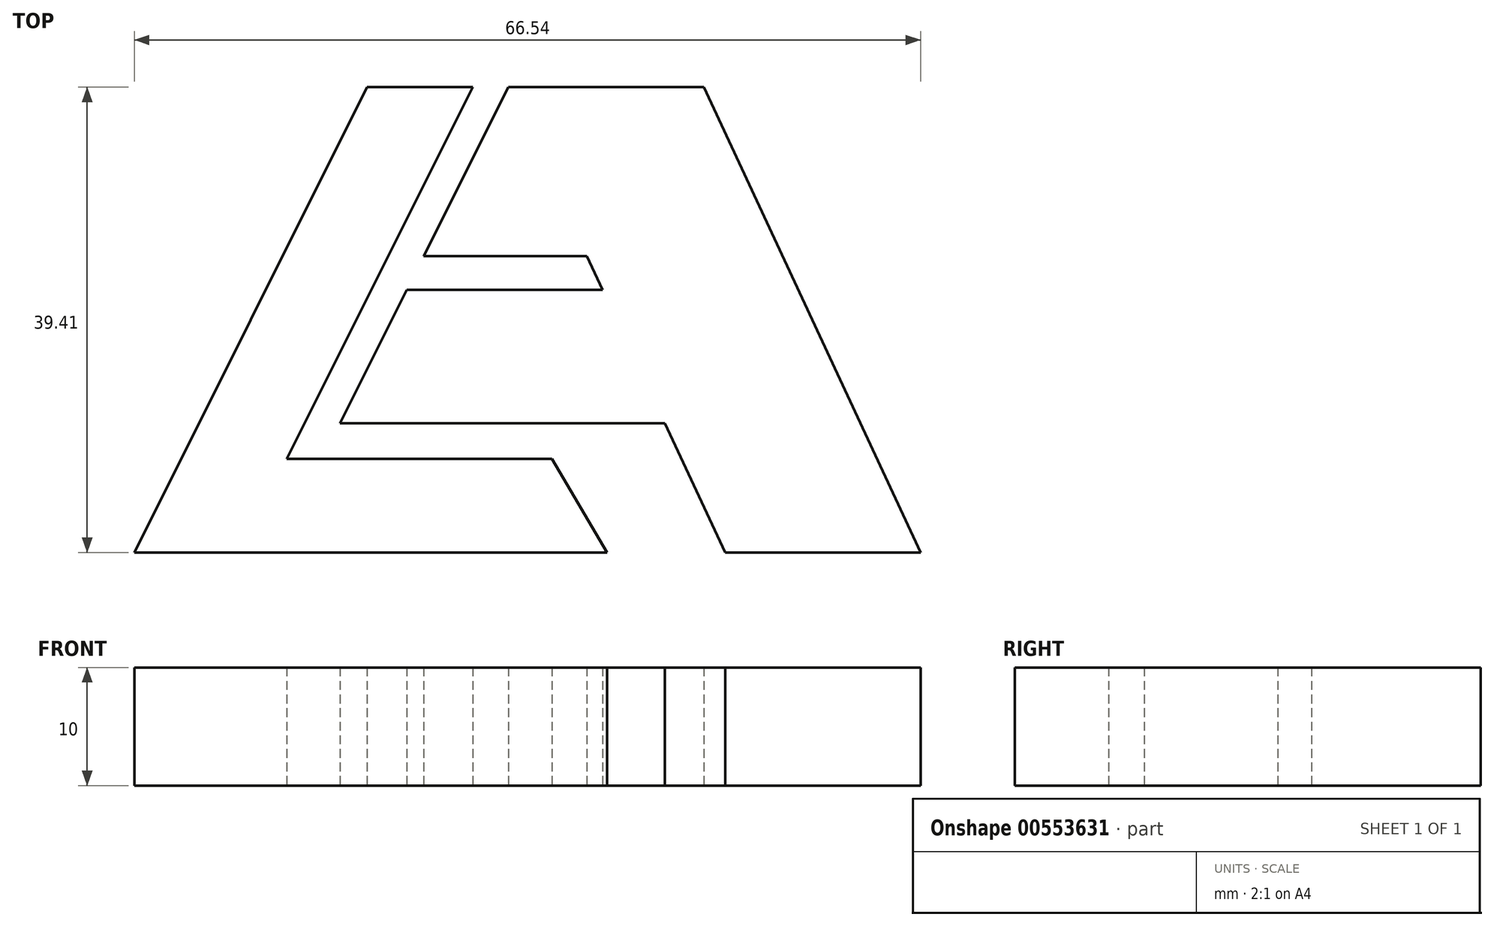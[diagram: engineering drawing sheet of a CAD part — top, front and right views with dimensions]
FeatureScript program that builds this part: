
annotation { "Feature Type Name" : "Feature", "Feature Type Description" : "" }
export const myFeature = defineFeature(function(context is Context, id is Id, definition is map)
    precondition{}
    {
        {
            var Q0;
            Q0=qCreatedBy(makeId("Top.planeOp"),FACE);
            var sketch = newSketch(context, id + "F0", { "sketchPlane" : qUnion([Q0])});
            skLineSegment(sketch, "E0.bottom", {"start": v(50, -25) * mm, "end": v(-50, -25) * mm, "construction": true});
            skLineSegment(sketch, "E0.top", {"start": v(50, 25) * mm, "end": v(-50, 25) * mm, "construction": true});
            skLineSegment(sketch, "E0.left", {"start": v(50, -25) * mm, "end": v(50, 25) * mm, "construction": true});
            skLineSegment(sketch, "E0.right", {"start": v(-50, -25) * mm, "end": v(-50, 25) * mm, "construction": true});
            skPoint(sketch, "E0.middle", {"position": v(0, 0) * mm});
            skLineSegment(sketch, "E1.0", {"start": v(-45.38, -20) * mm, "end": v(-45.67, 19.41) * mm, "construction": true});
            skLineSegment(sketch, "E1.1", {"start": v(45, -20) * mm, "end": v(-45.38, -20) * mm, "construction": true});
            skLineSegment(sketch, "E1.2", {"start": v(45, -20) * mm, "end": v(45, 19.41) * mm, "construction": true});
            skLineSegment(sketch, "E1.3", {"start": v(45, 19.41) * mm, "end": v(-45.67, 19.41) * mm, "construction": true});
            skPoint(sketch, "E2", {"position": v(-5.38, -20) * mm});
            skPoint(sketch, "E3", {"position": v(-25.67, 19.41) * mm});
            skLineSegment(sketch, "E4", {"start": v(-45.38, -20) * mm, "end": v(-25.67, 19.41) * mm});
            skLineSegment(sketch, "E5", {"start": v(-45.38, -20) * mm, "end": v(-5.38, -20) * mm});
            skLineSegment(sketch, "E6", {"start": v(-5.38, -20) * mm, "end": v(-10.02, -12.06) * mm});
            skLineSegment(sketch, "E7", {"start": v(-10.02, -12.06) * mm, "end": v(-32.47, -12.06) * mm});
            skLineSegment(sketch, "E8", {"start": v(-32.47, -12.06) * mm, "end": v(-16.73, 19.41) * mm});
            skLineSegment(sketch, "E9", {"start": v(-25.67, 19.41) * mm, "end": v(-16.73, 19.41) * mm});
            skPoint(sketch, "E10", {"position": v(-13.73, 19.41) * mm});
            skLineSegment(sketch, "E11", {"start": v(-13.73, 19.41) * mm, "end": v(-29.47, -12.06) * mm, "construction": true});
            skPoint(sketch, "E12", {"position": v(-20.89, 5.1) * mm});
            skLineSegment(sketch, "E13", {"start": v(-43.49, -9.06) * mm, "end": v(57.99, -9.06) * mm, "construction": true});
            skPoint(sketch, "E14", {"position": v(-29.47, -12.06) * mm});
            skPoint(sketch, "E15", {"position": v(-22.31, 2.25) * mm});
            skPoint(sketch, "E16", {"position": v(2.82, 19.41) * mm});
            skPoint(sketch, "E17", {"position": v(4.62, -20) * mm});
            skPoint(sketch, "E18", {"position": v(21.16, -20) * mm});
            skLineSegment(sketch, "E19", {"start": v(21.16, -20) * mm, "end": v(2.82, 19.41) * mm});
            skLineSegment(sketch, "E20", {"start": v(-13.73, 19.41) * mm, "end": v(2.82, 19.41) * mm});
            skLineSegment(sketch, "E21", {"start": v(-13.73, 19.41) * mm, "end": v(-20.89, 5.1) * mm});
            skPoint(sketch, "E22", {"position": v(-27.97, -9.06) * mm});
            skLineSegment(sketch, "E23", {"start": v(4.62, -20) * mm, "end": v(-26.38, 46.58) * mm, "construction": true});
            skLineSegment(sketch, "E24", {"start": v(-20.89, 5.1) * mm, "end": v(-7.07, 5.1) * mm});
            skLineSegment(sketch, "E25", {"start": v(-22.31, 2.25) * mm, "end": v(-5.74, 2.25) * mm});
            skLineSegment(sketch, "E26", {"start": v(-5.74, 2.25) * mm, "end": v(-7.07, 5.1) * mm});
            skLineSegment(sketch, "E27", {"start": v(-22.31, 2.25) * mm, "end": v(-27.97, -9.06) * mm});
            skLineSegment(sketch, "E28", {"start": v(-27.97, -9.06) * mm, "end": v(-0.47, -9.06) * mm});
            skLineSegment(sketch, "E29", {"start": v(-0.47, -9.06) * mm, "end": v(4.62, -20) * mm});
            skLineSegment(sketch, "E30", {"start": v(4.62, -20) * mm, "end": v(21.16, -20) * mm});
            skSolve(sketch);
        }
        {
            var Q0;
            Q0 = qSketchRegion(id + "F0", true);
            extrude(context, id + "F1", {"entities" : qUnion([Q0]), "depth" : 10 * mm, "offsetDistance" : 25 * mm});
        }
    });
